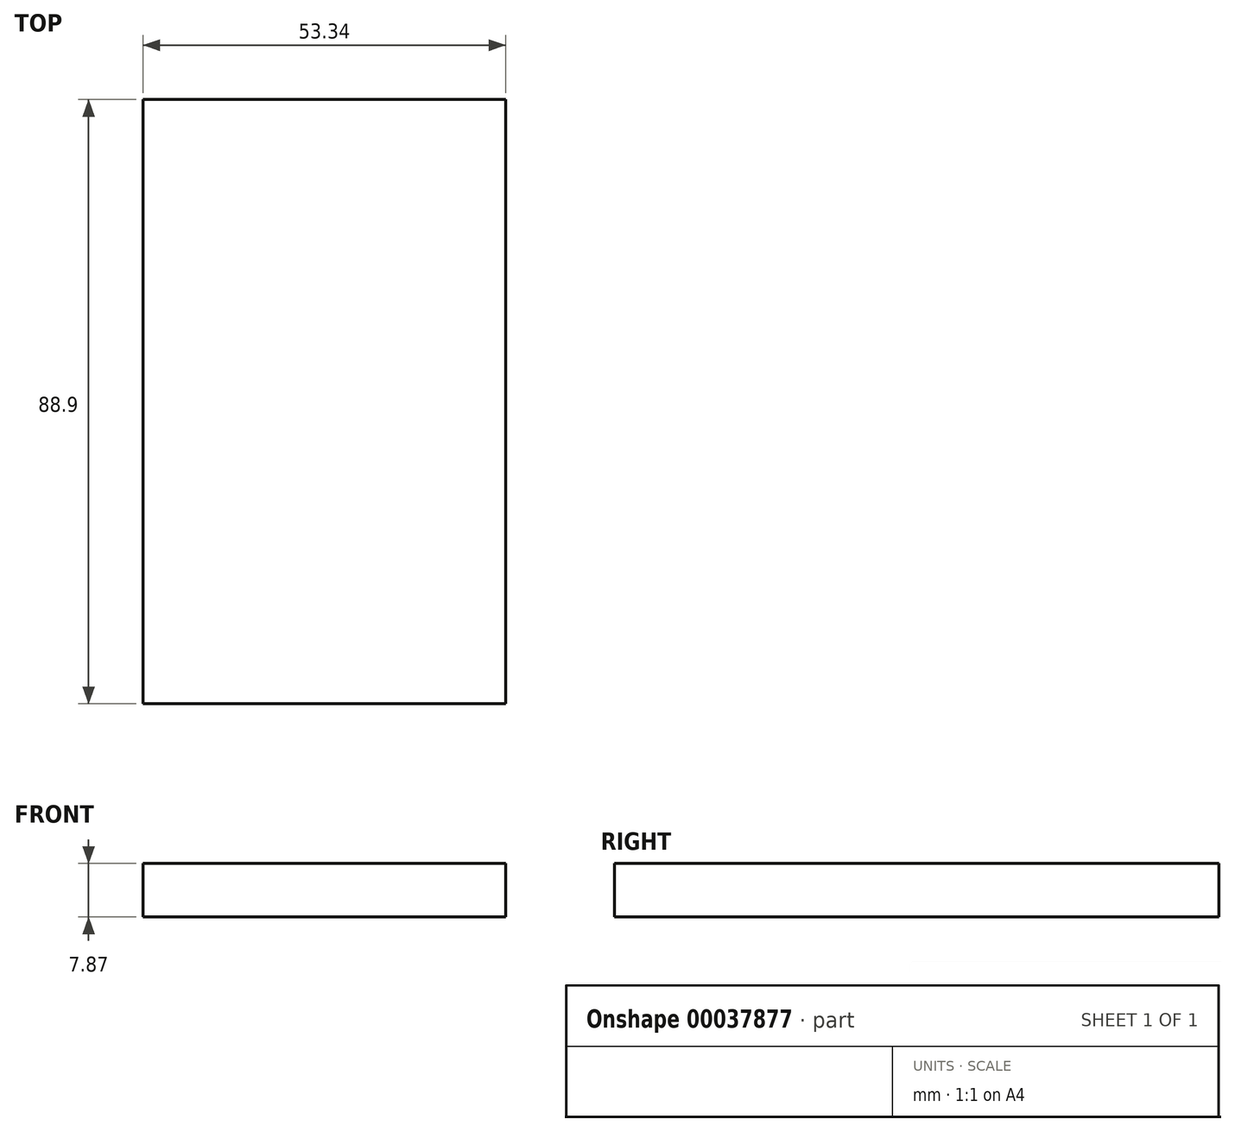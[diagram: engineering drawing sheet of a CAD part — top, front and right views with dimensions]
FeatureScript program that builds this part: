
annotation { "Feature Type Name" : "Feature", "Feature Type Description" : "" }
export const myFeature = defineFeature(function(context is Context, id is Id, definition is map)
    precondition{}
    {
        {
            var Q0;
            Q0=qCreatedBy(makeId("Top.planeOp"),FACE);
            var sketch = newSketch(context, id + "F0", { "sketchPlane" : qUnion([Q0])});
            skLineSegment(sketch, "E0.bottom", {"start": v(0, 0) * mm, "end": v(53.34, 0) * mm});
            skLineSegment(sketch, "E0.top", {"start": v(0, -88.9) * mm, "end": v(53.34, -88.9) * mm});
            skLineSegment(sketch, "E0.left", {"start": v(0, 0) * mm, "end": v(0, -88.9) * mm});
            skLineSegment(sketch, "E0.right", {"start": v(53.34, 0) * mm, "end": v(53.34, -88.9) * mm});
            skSolve(sketch);
        }
        {
            var Q0;
            Q0 = qSketchRegion(id + "F0", true);
            extrude(context, id + "F1", {"entities" : qUnion([Q0]), "depth" : 7.87 * mm});
        }
    });
